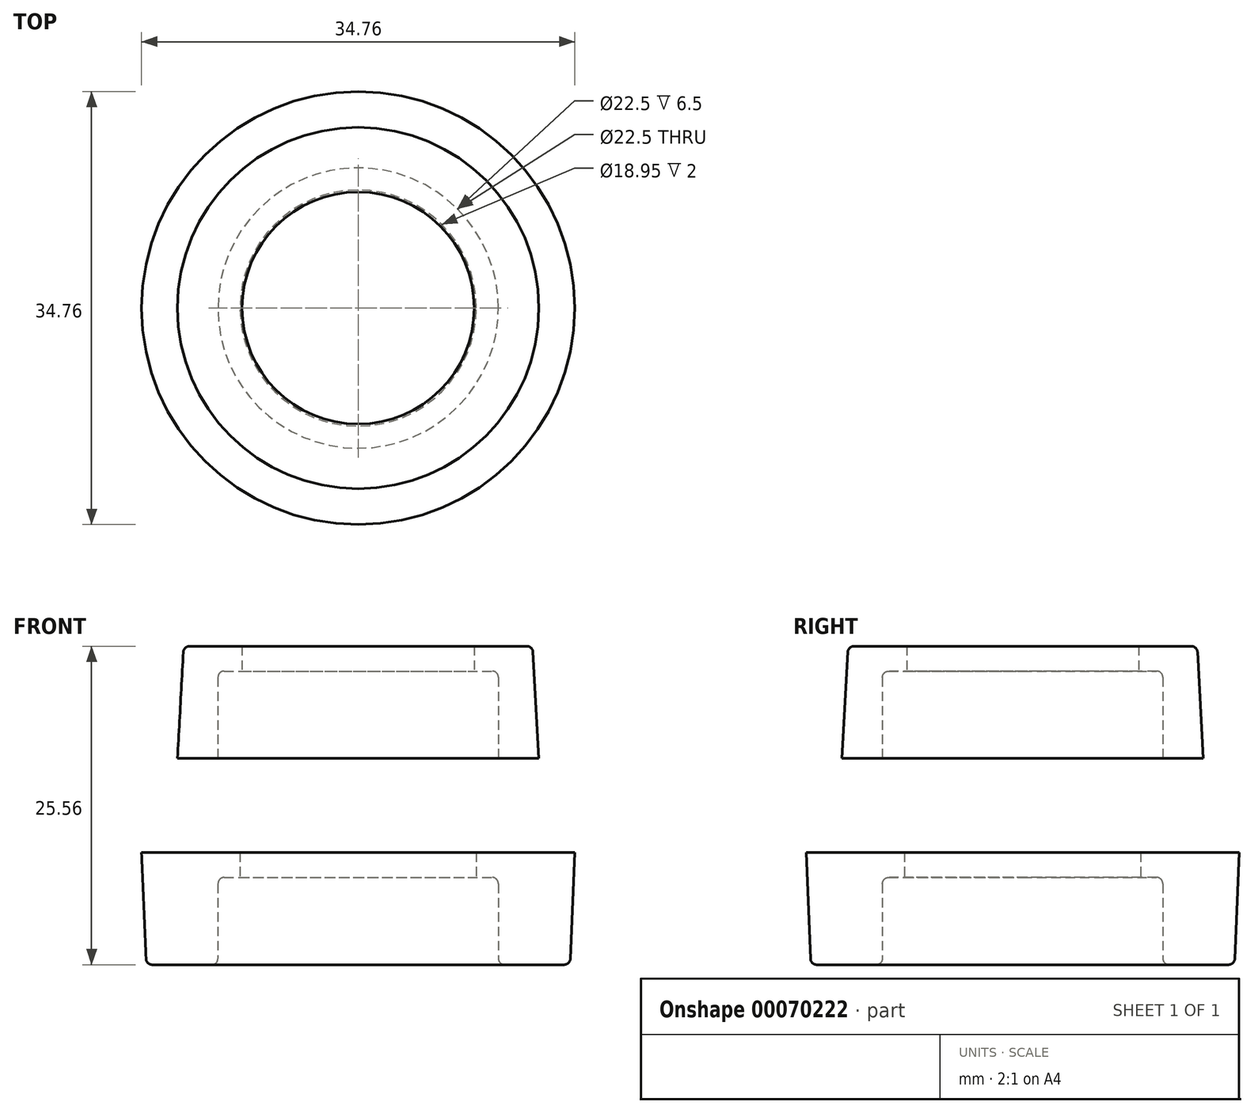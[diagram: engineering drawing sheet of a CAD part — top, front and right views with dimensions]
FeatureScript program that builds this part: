
annotation { "Feature Type Name" : "Feature", "Feature Type Description" : "" }
export const myFeature = defineFeature(function(context is Context, id is Id, definition is map)
    precondition{}
    {
        {
            var Q0;
            Q0=qCreatedBy(makeId("Front.planeOp"),FACE);
            var sketch = newSketch(context, id + "F0", { "sketchPlane" : qUnion([Q0])});
            skLineSegment(sketch, "E0", {"start": v(0, 0) * mm, "end": v(0, 20.93) * mm, "construction": true});
            skLineSegment(sketch, "E1", {"start": v(-11.25, 0) * mm, "end": v(-11.25, 6.5) * mm});
            skLineSegment(sketch, "E2", {"start": v(-11.3, 9) * mm, "end": v(-13.53, 9) * mm});
            skLineSegment(sketch, "E3", {"start": v(-14.03, 8.53) * mm, "end": v(-14.5, 0) * mm});
            skLineSegment(sketch, "E4", {"start": v(-14.5, 0) * mm, "end": v(-11.25, 0) * mm});
            skLineSegment(sketch, "E5.bottom", {"start": v(-11.3, 9) * mm, "end": v(-9.3, 9) * mm});
            skLineSegment(sketch, "E5.top", {"start": v(-10.75, 7) * mm, "end": v(-9.3, 7) * mm});
            skLineSegment(sketch, "E5.right", {"start": v(-9.3, 9) * mm, "end": v(-9.3, 7) * mm});
            skArc(sketch, "E6.filletArc", {"start": v(-10.75, 7) * mm, "mid": v(-11.1, 6.85) * mm, "end": v(-11.25, 6.5) * mm});
            skPoint(sketch, "E7.visualSharp", {"position": v(-14, 9) * mm});
            skArc(sketch, "E7.filletArc", {"start": v(-13.53, 9) * mm, "mid": v(-13.87, 8.86) * mm, "end": v(-14.03, 8.53) * mm});
            skLineSegment(sketch, "E8", {"start": v(-11.25, -10.06) * mm, "end": v(-11.25, -16.06) * mm});
            skLineSegment(sketch, "E9", {"start": v(-11.75, -16.56) * mm, "end": v(-16.52, -16.56) * mm});
            skLineSegment(sketch, "E10", {"start": v(-17.02, -16.08) * mm, "end": v(-17.38, -7.56) * mm});
            skLineSegment(sketch, "E11", {"start": v(-17.38, -7.56) * mm, "end": v(-9.48, -7.56) * mm});
            skLineSegment(sketch, "E12", {"start": v(-9.48, -7.56) * mm, "end": v(-9.48, -9.56) * mm});
            skLineSegment(sketch, "E13", {"start": v(-9.48, -9.56) * mm, "end": v(-10.75, -9.56) * mm});
            skPoint(sketch, "E14.visualSharp", {"position": v(-11.25, -9.56) * mm});
            skArc(sketch, "E14.filletArc", {"start": v(-10.75, -9.56) * mm, "mid": v(-11.1, -9.7) * mm, "end": v(-11.25, -10.06) * mm});
            skPoint(sketch, "E15.visualSharp", {"position": v(-17, -16.56) * mm});
            skArc(sketch, "E15.filletArc", {"start": v(-17.02, -16.08) * mm, "mid": v(-16.87, -16.42) * mm, "end": v(-16.52, -16.56) * mm});
            skPoint(sketch, "E16.visualSharp", {"position": v(-11.25, -16.56) * mm});
            skArc(sketch, "E16.filletArc", {"start": v(-11.75, -16.56) * mm, "mid": v(-11.4, -16.41) * mm, "end": v(-11.25, -16.06) * mm});
            skSolve(sketch);
        }
        {
            var Q0;
            Q0=makeQuery(id+"F0.imprint","IMPRINT",FACE,{"disambiguationData":[TD([[makeQuery(id+"F0.imprint","IMPRINT",EDGE,{"derivedFrom":sQuery(id+"F0.wireOp",EDGE,"E1")}),1.0]])]});
            var Q1;
            Q1=makeQuery(id+"F0.imprint","IMPRINT",FACE,{"disambiguationData":[TD([[makeQuery(id+"F0.imprint","IMPRINT",EDGE,{"derivedFrom":sQuery(id+"F0.wireOp",EDGE,"E8")}),-1.0]])]});
            var Q2;
            Q2=sQuery(id+"F0.wireOp",EDGE,"E0");
            revolve(context, id + "F1", {"entities" : qUnion([Q0, Q1]), "axis" : qUnion([Q2]), "revolveType" : RevolveType.FULL});
        }
    });
